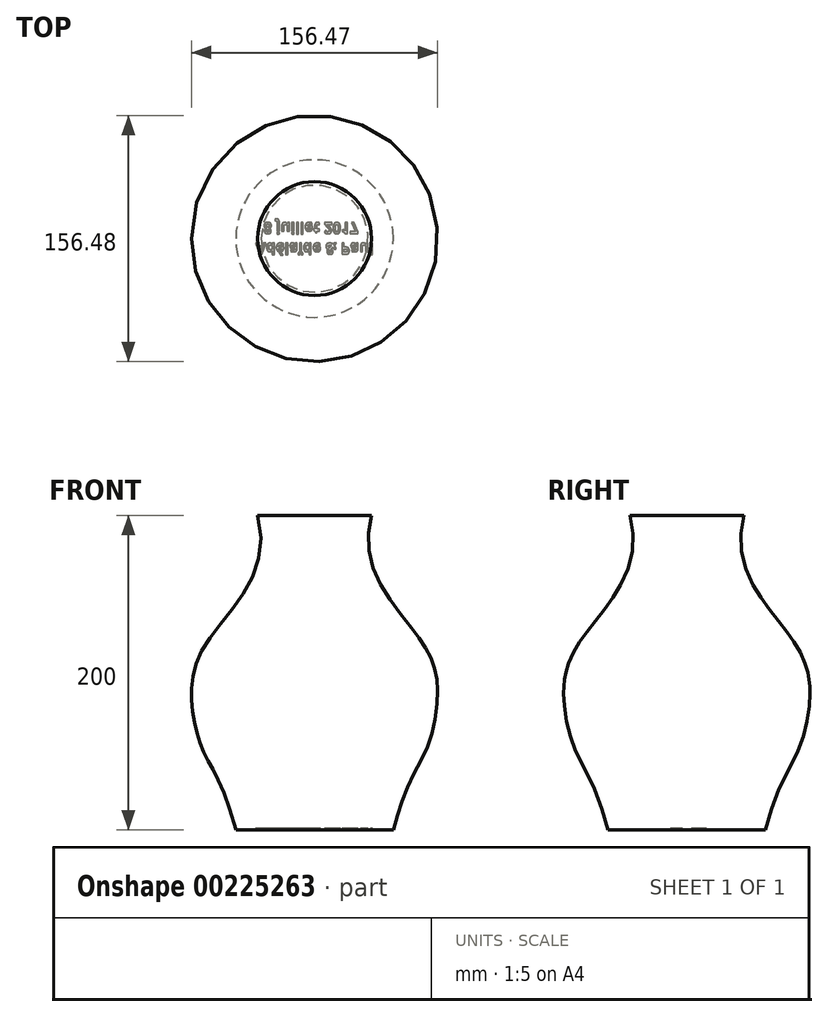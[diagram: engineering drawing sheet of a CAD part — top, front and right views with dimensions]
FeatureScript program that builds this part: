
annotation { "Feature Type Name" : "Feature", "Feature Type Description" : "" }
export const myFeature = defineFeature(function(context is Context, id is Id, definition is map)
    precondition{}
    {
        {
            var Q0;
            Q0=qCreatedBy(makeId("Front.planeOp"),FACE);
            var sketch = newSketch(context, id + "F0", { "sketchPlane" : qUnion([Q0])});
            skFitSpline(sketch, "E0", {"points": [v(-50, 0) * mm, v(-70, 48.83) * mm, v(-77.58, 76.9) * mm, v(-70, 116.65) * mm, v(-36.13, 200) * mm], "startDerivative": vector(-88.83, 347.26) * mm, "endDerivative": vector(-93.38, 350.48) * mm});
            skLineSegment(sketch, "E1", {"start": v(-50, 0) * mm, "end": v(0, 0) * mm});
            skLineSegment(sketch, "E2", {"start": v(0, 0) * mm, "end": v(0, 298.77) * mm, "construction": true});
            skLineSegment(sketch, "E3", {"start": v(-36.13, 200) * mm, "end": v(0, 200) * mm});
            skLineSegment(sketch, "E4", {"start": v(0, 200) * mm, "end": v(0, 0) * mm});
            skLineSegment(sketch, "E5", {"start": v(-70, 289.61) * mm, "end": v(-70, 10.48) * mm, "construction": true});
            skSolve(sketch);
        }
        {
            var Q0;
            Q0 = qSketchRegion(id + "F0", true);
            var Q1;
            Q1=sQuery(id+"F0.wireOp",EDGE,"E2");
            revolve(context, id + "F1", {"surfaceOperationType" : NewSurfaceOperationType.NEW, "entities" : qUnion([Q0]), "axis" : qUnion([Q1]), "revolveType" : RevolveType.FULL});
        }
        {
            var Q0;
            Q0=makeQuery(id+"F1.opRevolve","SWEPT_FACE",FACE,{"disambiguationData":[OSD([sQuery(id+"F0.wireOp",EDGE,"E1")])]});
            var sketch = newSketch(context, id + "F2", { "sketchPlane" : qUnion([Q0])});
            skText(sketch, "E6", { "text": "Adélaïde & Paul\n  8 juillet 2017", "fontName": "OpenSans-Bold.ttf"});
            const initialGuessF2  = {"E6": [-0.0375, 0.003, 1, 0, 0.00692]};
            skSetInitialGuess(sketch, initialGuessF2);
            skSolve(sketch);
        }
        {
            var Q0;
            Q0 = qSketchRegion(id + "F2", true);
            extrude(context, id + "F3", {"entities" : qUnion([Q0]), "operationType" : NewBodyOperationType.REMOVE, "oppositeDirection" : true, "depth" : 1 * mm, "offsetDistance" : 25 * mm});
        }
    });
